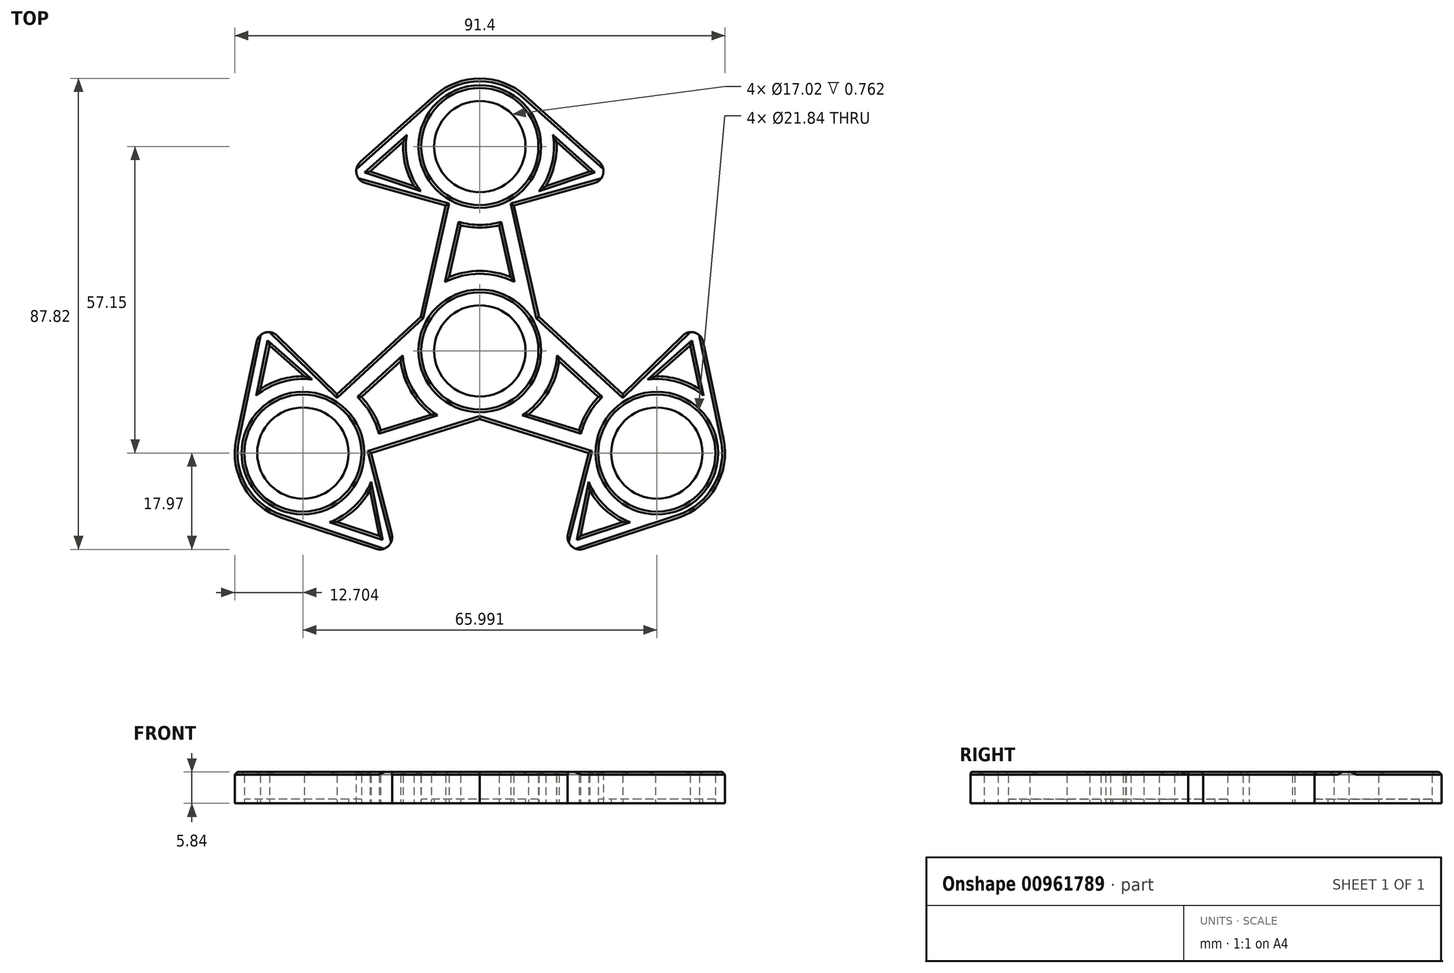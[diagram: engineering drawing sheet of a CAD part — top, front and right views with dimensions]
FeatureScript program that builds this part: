
annotation { "Feature Type Name" : "Feature", "Feature Type Description" : "" }
export const myFeature = defineFeature(function(context is Context, id is Id, definition is map)
    precondition{}
    {
        {
            var Q0;
            Q0=qCreatedBy(makeId("Top.planeOp"),FACE);
            var sketch = newSketch(context, id + "F0", { "sketchPlane" : qUnion([Q0])});
            skCircle(sketch, "E0", {"center": v(0, 0) * mm, "radius": 10.92 * mm});
            skCircle(sketch, "E1", {"center": v(0, 38.1) * mm, "radius": 10.92 * mm});
            skArc(sketch, "E2", {"start": v(8.46, 47.57) * mm, "mid": v(0, 50.8) * mm, "end": v(-8.46, 47.57) * mm});
            skCircle(sketch, "E3.1.1", {"center": v(-33, -19.05) * mm, "radius": 10.92 * mm});
            skArc(sketch, "E3.1.3", {"start": v(-45.43, -16.45) * mm, "mid": v(-44, -25.4) * mm, "end": v(-36.96, -31.11) * mm});
            skCircle(sketch, "E3.2.1", {"center": v(33, -19.05) * mm, "radius": 10.92 * mm});
            skArc(sketch, "E3.2.3", {"start": v(36.96, -31.11) * mm, "mid": v(44, -25.4) * mm, "end": v(45.43, -16.45) * mm});
            skLineSegment(sketch, "E4", {"start": v(0, 0) * mm, "end": v(0, 38.1) * mm});
            skLineSegment(sketch, "E5", {"start": v(-25.4, 32.43) * mm, "end": v(-8.46, 47.57) * mm});
            skLineSegment(sketch, "E6", {"start": v(8.46, 47.57) * mm, "end": v(25.4, 32.43) * mm});
            skLineSegment(sketch, "E7", {"start": v(25.4, 32.43) * mm, "end": v(6.35, 27.1) * mm});
            skLineSegment(sketch, "E8", {"start": v(-6.35, 27.1) * mm, "end": v(-25.4, 32.43) * mm});
            skLineSegment(sketch, "E9.1.0", {"start": v(-15.39, -38.21) * mm, "end": v(-36.96, -31.11) * mm});
            skLineSegment(sketch, "E9.2.0", {"start": v(40.79, 5.78) * mm, "end": v(45.43, -16.45) * mm});
            skLineSegment(sketch, "E10.1.0", {"start": v(-45.43, -16.45) * mm, "end": v(-40.79, 5.78) * mm});
            skLineSegment(sketch, "E10.2.0", {"start": v(36.96, -31.11) * mm, "end": v(15.39, -38.21) * mm});
            skLineSegment(sketch, "E11.1.0", {"start": v(-40.79, 5.78) * mm, "end": v(-26.65, -8.05) * mm});
            skLineSegment(sketch, "E11.2.0", {"start": v(15.39, -38.21) * mm, "end": v(20.3, -19.05) * mm});
            skLineSegment(sketch, "E12.1.0", {"start": v(-20.3, -19.05) * mm, "end": v(-15.39, -38.21) * mm});
            skLineSegment(sketch, "E12.2.0", {"start": v(26.65, -8.05) * mm, "end": v(40.79, 5.78) * mm});
            skLineSegment(sketch, "E13", {"start": v(-6.35, 27.1) * mm, "end": v(-11, 6.35) * mm});
            skLineSegment(sketch, "E14", {"start": v(-11, 6.35) * mm, "end": v(-26.65, -8.05) * mm});
            skLineSegment(sketch, "E15", {"start": v(-20.3, -19.05) * mm, "end": v(0, -12.7) * mm});
            skLineSegment(sketch, "E16", {"start": v(0, -12.7) * mm, "end": v(20.3, -19.05) * mm});
            skLineSegment(sketch, "E17", {"start": v(26.65, -8.05) * mm, "end": v(11, 6.35) * mm});
            skLineSegment(sketch, "E18", {"start": v(11, 6.35) * mm, "end": v(6.35, 27.1) * mm});
            skLineSegment(sketch, "E19", {"start": v(-14.29, 39.01) * mm, "end": v(-20.47, 33.49) * mm});
            skLineSegment(sketch, "E20", {"start": v(-20.47, 33.49) * mm, "end": v(-12.27, 30.72) * mm});
            skLineSegment(sketch, "E21", {"start": v(12.27, 30.72) * mm, "end": v(20.47, 33.49) * mm});
            skLineSegment(sketch, "E22", {"start": v(20.47, 33.49) * mm, "end": v(14.29, 39.01) * mm});
            skLineSegment(sketch, "E23.1.0", {"start": v(-26.64, -31.88) * mm, "end": v(-18.76, -34.47) * mm});
            skLineSegment(sketch, "E23.2.0", {"start": v(40.93, -7.13) * mm, "end": v(39.24, 0.98) * mm});
            skLineSegment(sketch, "E24.1.0", {"start": v(-18.76, -34.47) * mm, "end": v(-20.47, -25.98) * mm});
            skLineSegment(sketch, "E24.2.0", {"start": v(39.24, 0.98) * mm, "end": v(32.73, -4.73) * mm});
            skLineSegment(sketch, "E25.1.0", {"start": v(-39.24, 0.99) * mm, "end": v(-40.93, -7.13) * mm});
            skLineSegment(sketch, "E25.2.0", {"start": v(18.76, -34.47) * mm, "end": v(26.64, -31.88) * mm});
            skLineSegment(sketch, "E26.1.0", {"start": v(-32.73, -4.73) * mm, "end": v(-39.24, 0.99) * mm});
            skLineSegment(sketch, "E26.2.0", {"start": v(20.47, -25.98) * mm, "end": v(18.76, -34.47) * mm});
            skLineSegment(sketch, "E27", {"start": v(-6.97, 24.32) * mm, "end": v(-7.06, 24.34) * mm});
            skLineSegment(sketch, "E28", {"start": v(6.97, 24.32) * mm, "end": v(7.06, 24.34) * mm});
            skArc(sketch, "E29", {"start": v(5.76, 13.75) * mm, "mid": v(0, 14.9) * mm, "end": v(-5.76, 13.75) * mm});
            skArc(sketch, "E30", {"start": v(-14.29, 39.01) * mm, "mid": v(-13.91, 34.7) * mm, "end": v(-12.27, 30.72) * mm});
            skArc(sketch, "E31.trimOffspring", {"start": v(12.27, 30.72) * mm, "mid": v(13.91, 34.71) * mm, "end": v(14.29, 39.01) * mm});
            skPoint(sketch, "E32.end.orphan", {"position": v(7.06, 23.94) * mm});
            skArc(sketch, "E33.trimOffspring", {"start": v(-3.59, 23.42) * mm, "mid": v(0, 23) * mm, "end": v(3.59, 23.42) * mm});
            skPoint(sketch, "E34.end.orphan", {"position": v(-7.06, 23.94) * mm});
            skPoint(sketch, "E35.orphan", {"position": v(13.84, 39.41) * mm});
            skPoint(sketch, "E36.orphan", {"position": v(-13.85, 39.4) * mm});
            skPoint(sketch, "E37.orphan", {"position": v(0, 30.72) * mm});
            skArc(sketch, "E38.trimOffspring", {"start": v(-14.78, -1.89) * mm, "mid": v(-12.9, -7.45) * mm, "end": v(-9.03, -11.86) * mm});
            skPoint(sketch, "E39.orphan", {"position": v(14.9, 0.4) * mm});
            skPoint(sketch, "E40.orphan", {"position": v(60.72, 26.83) * mm});
            skPoint(sketch, "E41.orphan", {"position": v(13.64, -1.78) * mm});
            skPoint(sketch, "E42.orphan", {"position": v(8.36, -10.92) * mm});
            skArc(sketch, "E43.trimOffspring", {"start": v(9.03, -11.86) * mm, "mid": v(12.9, -7.45) * mm, "end": v(14.78, -1.89) * mm});
            skPoint(sketch, "E44.orphan", {"position": v(-15.79, 1.94) * mm});
            skPoint(sketch, "E45.orphan", {"position": v(-8.36, -10.92) * mm});
            skPoint(sketch, "E46.orphan", {"position": v(-23.38, -7.4) * mm});
            skArc(sketch, "E47.1.0", {"start": v(-26.64, -31.88) * mm, "mid": v(-23.1, -29.4) * mm, "end": v(-20.47, -25.98) * mm});
            skArc(sketch, "E47.2.0", {"start": v(40.93, -7.13) * mm, "mid": v(37.01, -5.3) * mm, "end": v(32.73, -4.73) * mm});
            skArc(sketch, "E48.1.0", {"start": v(-32.73, -4.73) * mm, "mid": v(-37.02, -5.3) * mm, "end": v(-40.93, -7.13) * mm});
            skArc(sketch, "E48.2.0", {"start": v(20.47, -25.98) * mm, "mid": v(23.1, -29.4) * mm, "end": v(26.64, -31.88) * mm});
            skArc(sketch, "E49.1.0", {"start": v(-18.5, -14.82) * mm, "mid": v(-19.91, -11.5) * mm, "end": v(-22.08, -8.6) * mm});
            skArc(sketch, "E49.2.0", {"start": v(22.08, -8.6) * mm, "mid": v(19.91, -11.5) * mm, "end": v(18.5, -14.82) * mm});
            skPoint(sketch, "E50.orphan", {"position": v(-41.05, -7.72) * mm});
            skPoint(sketch, "E51.orphan", {"position": v(-27.2, -31.7) * mm});
            skPoint(sketch, "E52.orphan", {"position": v(27.2, -31.7) * mm});
            skPoint(sketch, "E53.orphan", {"position": v(41.05, -7.71) * mm});
            skLineSegment(sketch, "E54", {"start": v(-3.59, 23.42) * mm, "end": v(-5.76, 13.75) * mm});
            skLineSegment(sketch, "E55", {"start": v(3.59, 23.42) * mm, "end": v(5.76, 13.75) * mm});
            skPoint(sketch, "E56.orphan", {"position": v(-5.28, 23.94) * mm});
            skPoint(sketch, "E57.orphan", {"position": v(5.28, 23.94) * mm});
            skLineSegment(sketch, "E58.1.0", {"start": v(-18.5, -14.82) * mm, "end": v(-9.03, -11.86) * mm});
            skLineSegment(sketch, "E58.2.0", {"start": v(22.08, -8.6) * mm, "end": v(14.78, -1.89) * mm});
            skLineSegment(sketch, "E59.1.0", {"start": v(-22.08, -8.6) * mm, "end": v(-14.78, -1.89) * mm});
            skLineSegment(sketch, "E59.2.0", {"start": v(18.5, -14.82) * mm, "end": v(9.03, -11.86) * mm});
            skPoint(sketch, "E60.orphan", {"position": v(-18.1, -16.54) * mm});
            skPoint(sketch, "E61.orphan", {"position": v(23.38, -7.4) * mm});
            skPoint(sketch, "E62.orphan", {"position": v(18.1, -16.54) * mm});
            skCircle(sketch, "E63", {"center": v(0, 0) * mm, "radius": 8.5 * mm});
            skCircle(sketch, "E64", {"center": v(33, -19.05) * mm, "radius": 8.5 * mm});
            skCircle(sketch, "E65", {"center": v(-33, -19.05) * mm, "radius": 8.5 * mm});
            skCircle(sketch, "E66", {"center": v(0, 38.1) * mm, "radius": 8.5 * mm});
            skSolve(sketch);
        }
        {
            var Q0;
            Q0=makeQuery(id+"F0.imprint","IMPRINT",FACE,{"disambiguationData":[TD([[makeQuery(id+"F0.imprint","IMPRINT",EDGE,{"derivedFrom":sQuery(id+"F0.wireOp",EDGE,"E0")}),1.0]])]});
            var Q1;
            Q1=makeQuery(id+"F0.imprint","IMPRINT",FACE,{"disambiguationData":[TD([[makeQuery(id+"F0.imprint","IMPRINT",EDGE,{"derivedFrom":sQuery(id+"F0.wireOp",EDGE,"E3.2.1")}),1.0]])]});
            var Q2;
            Q2=makeQuery(id+"F0.imprint","IMPRINT",FACE,{"disambiguationData":[TD([[makeQuery(id+"F0.imprint","IMPRINT",EDGE,{"derivedFrom":sQuery(id+"F0.wireOp",EDGE,"E1")}),1.0]])]});
            var Q3;
            Q3=makeQuery(id+"F0.imprint","IMPRINT",FACE,{"disambiguationData":[TD([[makeQuery(id+"F0.imprint","IMPRINT",EDGE,{"derivedFrom":sQuery(id+"F0.wireOp",EDGE,"E3.1.1")}),1.0]])]});
            extrude(context, id + "F1", {"entities" : qUnion([Q0, Q1, Q2, Q3]), "depth" : 0.76 * mm, "offsetDistance" : 25.4 * mm});
        }
        {
            var Q0;
            Q0=makeQuery(id+"F0.imprint","IMPRINT",FACE,{"disambiguationData":[TD([[makeQuery(id+"F0.imprint","IMPRINT",EDGE,{"derivedFrom":sQuery(id+"F0.wireOp",EDGE,"E0")}),-1.0]])]});
            var Q1;
            {var subQ0=sQuery(id+"F0.wireOp",EDGE,"E3.2.2");Q1=makeQuery(id+"F0.imprint","IMPRINT",FACE,{"disambiguationData":[TD([[makeQuery(id+"F0.imprint","IMPRINT",EDGE,{"derivedFrom":subQ0}),1.0]])]});}
            var Q2;
            {var subQ0=sQuery(id+"F0.wireOp",EDGE,"qAN6bfDQ-EvD6-PB0c-LLV5-TB6usP3qM8oL");Q2=makeQuery(id+"F0.imprint","IMPRINT",FACE,{"disambiguationData":[TD([[makeQuery(id+"F0.imprint","IMPRINT",EDGE,{"derivedFrom":subQ0}),1.0]])]});}
            var Q3;
            {var subQ0=sQuery(id+"F0.wireOp",EDGE,"E3.1.2");Q3=makeQuery(id+"F0.imprint","IMPRINT",FACE,{"disambiguationData":[TD([[makeQuery(id+"F0.imprint","IMPRINT",EDGE,{"derivedFrom":subQ0}),1.0]])]});}
            var Q4;
            {var subQ0=sQuery(id+"F0.wireOp",EDGE,"9fF8XZbd-x6Pi-r7dD-wS89-5iYDqfJ158Ww");Q4=makeQuery(id+"F0.imprint","IMPRINT",FACE,{"disambiguationData":[TD([[makeQuery(id+"F0.imprint","IMPRINT",EDGE,{"derivedFrom":subQ0}),-1.0]])]});}
            var Q5;
            {var subQ0=sQuery(id+"F0.wireOp",EDGE,"6K4n1ReX-d9US-5ZDi-A2DK-j992RhachGyF");Q5=makeQuery(id+"F0.imprint","IMPRINT",FACE,{"disambiguationData":[TD([[makeQuery(id+"F0.imprint","IMPRINT",EDGE,{"derivedFrom":subQ0}),1.0]])]});}
            var Q6;
            Q6=makeQuery(id+"F0.imprint","IMPRINT",FACE,{"disambiguationData":[TD([[makeQuery(id+"F0.imprint","IMPRINT",EDGE,{"derivedFrom":sQuery(id+"F0.wireOp",EDGE,"E2")}),1.0]])]});
            var Q7;
            {var subQ0=sQuery(id+"F0.wireOp",EDGE,"9fF8XZbd-x6Pi-r7dD-wS89-5iYDqfJ158Ww");Q7=makeQuery(id+"F0.imprint","IMPRINT",FACE,{"disambiguationData":[TD([[makeQuery(id+"F0.imprint","IMPRINT",EDGE,{"derivedFrom":subQ0}),1.0]])]});}
            var Q8;
            {var subQ0=sQuery(id+"F0.wireOp",EDGE,"qAN6bfDQ-EvD6-PB0c-LLV5-TB6usP3qM8oL");Q8=makeQuery(id+"F0.imprint","IMPRINT",FACE,{"disambiguationData":[TD([[makeQuery(id+"F0.imprint","IMPRINT",EDGE,{"derivedFrom":subQ0}),-1.0]])]});}
            var Q9;
            {var subQ0=sQuery(id+"F0.wireOp",EDGE,"Vkq1GlN2-p2l9-0JIi-93ZN-x3V1hNP8lanI");var subQ1=sQuery(id+"F0.wireOp",EDGE,"OuJw4BYg-WvBj-6tcM-ZUpN-g2h8ElnBMkLZ");var subQ2=makeQuery(id+"F0.imprint","INTERSECT",VERTEX,{"derivedFrom":[subQ1,subQ0]});Q9=makeQuery(id+"F0.imprint","IMPRINT",FACE,{"disambiguationData":[TD([[makeQuery(id+"F0.imprint","IMPRINT",EDGE,{"disambiguationData":[TD([[subQ2,-1.0]])],"derivedFrom":subQ0}),1.0]])]});}
            var Q10;
            {var subQ1=sQuery(id+"F0.wireOp",EDGE,"45f8ba8a-7cd9-4461-8c1c-9691e63ae262.trimOffspring");var subQ5=sQuery(id+"F0.wireOp",EDGE,"TcN3lwoU-SvPN-Eq9K-OPf6-Ab366GjWDurW");var subQ8=makeQuery(id+"F0.imprint","INTERSECT",VERTEX,{"derivedFrom":[subQ5,subQ1]});Q10=makeQuery(id+"F0.imprint","IMPRINT",FACE,{"disambiguationData":[TD([[makeQuery(id+"F0.imprint","IMPRINT",EDGE,{"disambiguationData":[TD([[subQ8,-1.0]])],"derivedFrom":subQ5}),-1.0]])]});}
            var Q11;
            Q11=makeQuery(id+"F0.imprint","IMPRINT",FACE,{"disambiguationData":[TD([[makeQuery(id+"F0.imprint","IMPRINT",EDGE,{"derivedFrom":sQuery(id+"F0.wireOp",EDGE,"E5")}),-1.0]])]});
            var Q12;
            Q12=makeQuery(id+"F0.imprint","IMPRINT",FACE,{"disambiguationData":[TD([[makeQuery(id+"F0.imprint","IMPRINT",EDGE,{"derivedFrom":sQuery(id+"F0.wireOp",EDGE,"E6")}),-1.0]])]});
            var Q13;
            {var subQ0=sQuery(id+"F0.wireOp",EDGE,"PzGggORM-jraf-rS0D-nCfz-ZiBeTToQzrcL");Q13=makeQuery(id+"F0.imprint","IMPRINT",FACE,{"disambiguationData":[TD([[makeQuery(id+"F0.imprint","IMPRINT",EDGE,{"derivedFrom":subQ0}),1.0]])]});}
            var Q14;
            Q14=makeQuery(id+"F0.imprint","IMPRINT",FACE,{"disambiguationData":[TD([[makeQuery(id+"F0.imprint","IMPRINT",EDGE,{"derivedFrom":sQuery(id+"F0.wireOp",EDGE,"E3.2.1")}),-1.0]])]});
            var Q15;
            {var subQ3=sQuery(id+"F0.wireOp",EDGE,"9a17e62f-96f6-4f13-b012-882fd0498e39.2.0");var subQ5=sQuery(id+"F0.wireOp",EDGE,"06a4b1de-04c7-4eba-a49c-bad1cd3fa0e8.2.0");var subQ7=makeQuery(id+"F0.imprint","INTERSECT",VERTEX,{"derivedFrom":[subQ3,subQ5]});Q15=makeQuery(id+"F0.imprint","IMPRINT",FACE,{"disambiguationData":[TD([[makeQuery(id+"F0.imprint","IMPRINT",EDGE,{"disambiguationData":[TD([[subQ7,1.0]])],"derivedFrom":subQ3}),1.0]])]});}
            var Q16;
            Q16=makeQuery(id+"F0.imprint","IMPRINT",FACE,{"disambiguationData":[TD([[makeQuery(id+"F0.imprint","IMPRINT",EDGE,{"derivedFrom":sQuery(id+"F0.wireOp",EDGE,"E3.1.1")}),-1.0]])]});
            var Q17;
            {var subQ3=sQuery(id+"F0.wireOp",EDGE,"9a17e62f-96f6-4f13-b012-882fd0498e39.1.0");var subQ5=sQuery(id+"F0.wireOp",EDGE,"06a4b1de-04c7-4eba-a49c-bad1cd3fa0e8.1.0");var subQ7=makeQuery(id+"F0.imprint","INTERSECT",VERTEX,{"derivedFrom":[subQ3,subQ5]});Q17=makeQuery(id+"F0.imprint","IMPRINT",FACE,{"disambiguationData":[TD([[makeQuery(id+"F0.imprint","IMPRINT",EDGE,{"disambiguationData":[TD([[subQ7,1.0]])],"derivedFrom":subQ3}),1.0]])]});}
            var Q18;
            {var subQ2=sQuery(id+"F0.wireOp",EDGE,"E3.1.0");var subQ5=sQuery(id+"F0.wireOp",EDGE,"OuJw4BYg-WvBj-6tcM-ZUpN-g2h8ElnBMkLZ");var subQ8=makeQuery(id+"F0.imprint","INTERSECT",VERTEX,{"derivedFrom":[subQ5,subQ2]});Q18=makeQuery(id+"F0.imprint","IMPRINT",FACE,{"disambiguationData":[TD([[makeQuery(id+"F0.imprint","IMPRINT",EDGE,{"disambiguationData":[TD([[subQ8,-1.0]])],"derivedFrom":subQ2}),-1.0]])]});}
            var Q19;
            {var subQ3=sQuery(id+"F0.wireOp",EDGE,"Yt0YYVHN-KNV7-8yMq-8hyP-T0BDWzkc9sLh");Q19=makeQuery(id+"F0.imprint","IMPRINT",FACE,{"disambiguationData":[TD([[makeQuery(id+"F0.imprint","IMPRINT",EDGE,{"derivedFrom":subQ3}),-1.0]])]});}
            var Q20;
            {var subQ2=sQuery(id+"F0.wireOp",EDGE,"E3.2.0");var subQ5=sQuery(id+"F0.wireOp",EDGE,"e03ed8af-40f6-4605-b513-6e7bd98e8c99.trimOffspring");var subQ8=makeQuery(id+"F0.imprint","INTERSECT",VERTEX,{"derivedFrom":[subQ2,subQ5]});Q20=makeQuery(id+"F0.imprint","IMPRINT",FACE,{"disambiguationData":[TD([[makeQuery(id+"F0.imprint","IMPRINT",EDGE,{"disambiguationData":[TD([[subQ8,-1.0]])],"derivedFrom":subQ2}),-1.0]])]});}
            var Q21;
            {var subQ1=sQuery(id+"F0.wireOp",EDGE,"E13");var subQ3=sQuery(id+"F0.wireOp",EDGE,"E27");var subQ4=makeQuery(id+"F0.imprint","INTERSECT",VERTEX,{"derivedFrom":[subQ1,subQ3]});Q21=makeQuery(id+"F0.imprint","IMPRINT",FACE,{"disambiguationData":[TD([[makeQuery(id+"F0.imprint","IMPRINT",EDGE,{"disambiguationData":[TD([[subQ4,1.0]])],"derivedFrom":subQ3}),-1.0]])]});}
            var Q22;
            {var subQ0=sQuery(id+"F0.wireOp",EDGE,"E34");var subQ1=sQuery(id+"F0.wireOp",EDGE,"E13");var subQ2=makeQuery(id+"F0.imprint","INTERSECT",VERTEX,{"derivedFrom":[subQ1,subQ0]});Q22=makeQuery(id+"F0.imprint","IMPRINT",FACE,{"disambiguationData":[TD([[makeQuery(id+"F0.imprint","IMPRINT",EDGE,{"disambiguationData":[TD([[subQ2,1.0]])],"derivedFrom":subQ1}),1.0]])]});}
            var Q23;
            {var subQ0=sQuery(id+"F0.wireOp",EDGE,"E34");var subQ1=sQuery(id+"F0.wireOp",EDGE,"E13");var subQ2=makeQuery(id+"F0.imprint","INTERSECT",VERTEX,{"derivedFrom":[subQ1,subQ0]});Q23=makeQuery(id+"F0.imprint","IMPRINT",FACE,{"disambiguationData":[TD([[makeQuery(id+"F0.imprint","IMPRINT",EDGE,{"disambiguationData":[TD([[subQ2,-1.0]])],"derivedFrom":subQ1}),1.0]])]});}
            var Q24;
            {var subQ1=sQuery(id+"F0.wireOp",EDGE,"E34");var subQ3=sQuery(id+"F0.wireOp",EDGE,"b4e95768-ea4a-4253-9161-41f6c7fc2a35.trimOffspring");var subQ4=makeQuery(id+"F0.imprint","INTERSECT",VERTEX,{"derivedFrom":[subQ1,subQ3]});Q24=makeQuery(id+"F0.imprint","IMPRINT",FACE,{"disambiguationData":[TD([[makeQuery(id+"F0.imprint","IMPRINT",EDGE,{"disambiguationData":[TD([[subQ4,-1.0]])],"derivedFrom":subQ3}),-1.0]])]});}
            var Q25;
            {var subQ0=sQuery(id+"F0.wireOp",EDGE,"E32");var subQ1=sQuery(id+"F0.wireOp",EDGE,"E18");var subQ2=makeQuery(id+"F0.imprint","INTERSECT",VERTEX,{"derivedFrom":[subQ1,subQ0]});Q25=makeQuery(id+"F0.imprint","IMPRINT",FACE,{"disambiguationData":[TD([[makeQuery(id+"F0.imprint","IMPRINT",EDGE,{"disambiguationData":[TD([[subQ2,-1.0]])],"derivedFrom":subQ1}),1.0]])]});}
            var Q26;
            {var subQ1=sQuery(id+"F0.wireOp",EDGE,"E32");var subQ3=sQuery(id+"F0.wireOp",EDGE,"2032d7e4-90d3-44b6-8336-25ac22edd1a0.trimOffspring");var subQ4=makeQuery(id+"F0.imprint","INTERSECT",VERTEX,{"derivedFrom":[subQ1,subQ3]});Q26=makeQuery(id+"F0.imprint","IMPRINT",FACE,{"disambiguationData":[TD([[makeQuery(id+"F0.imprint","IMPRINT",EDGE,{"disambiguationData":[TD([[subQ4,-1.0]])],"derivedFrom":subQ3}),1.0]])]});}
            var Q27;
            {var subQ1=sQuery(id+"F0.wireOp",EDGE,"E18");var subQ3=sQuery(id+"F0.wireOp",EDGE,"E28");var subQ4=makeQuery(id+"F0.imprint","INTERSECT",VERTEX,{"derivedFrom":[subQ1,subQ3]});Q27=makeQuery(id+"F0.imprint","IMPRINT",FACE,{"disambiguationData":[TD([[makeQuery(id+"F0.imprint","IMPRINT",EDGE,{"disambiguationData":[TD([[subQ4,1.0]])],"derivedFrom":subQ3}),1.0]])]});}
            extrude(context, id + "F2", {"entities" : qUnion([Q0, Q1, Q2, Q3, Q4, Q5, Q6, Q7, Q8, Q9, Q10, Q11, Q12, Q13, Q14, Q15, Q16, Q17, Q18, Q19, Q20, Q21, Q22, Q23, Q24, Q25, Q26, Q27]), "depth" : 5.84 * mm, "offsetDistance" : 25.4 * mm});
        }
        {
            var Q0;
            Q0=makeQuery(id+"F2.opExtrude","CAP_FACE",FACE,{"disambiguationData":[OSD([sQuery(id+"F0.wireOp",EDGE,"E0"),sQuery(id+"F0.wireOp",EDGE,"E1"),sQuery(id+"F0.wireOp",EDGE,"E2"),sQuery(id+"F0.wireOp",EDGE,"E3.1.1"),sQuery(id+"F0.wireOp",EDGE,"E3.1.3"),sQuery(id+"F0.wireOp",EDGE,"E3.2.1"),sQuery(id+"F0.wireOp",EDGE,"E3.2.3"),sQuery(id+"F0.wireOp",EDGE,"E5"),sQuery(id+"F0.wireOp",EDGE,"E6"),sQuery(id+"F0.wireOp",EDGE,"E7"),sQuery(id+"F0.wireOp",EDGE,"E8"),sQuery(id+"F0.wireOp",EDGE,"E9.1.0"),sQuery(id+"F0.wireOp",EDGE,"E9.2.0"),sQuery(id+"F0.wireOp",EDGE,"E10.1.0"),sQuery(id+"F0.wireOp",EDGE,"E10.2.0"),sQuery(id+"F0.wireOp",EDGE,"E11.1.0"),sQuery(id+"F0.wireOp",EDGE,"E11.2.0"),sQuery(id+"F0.wireOp",EDGE,"E12.1.0"),sQuery(id+"F0.wireOp",EDGE,"E12.2.0"),sQuery(id+"F0.wireOp",EDGE,"E13"),sQuery(id+"F0.wireOp",EDGE,"E14"),sQuery(id+"F0.wireOp",EDGE,"E15"),sQuery(id+"F0.wireOp",EDGE,"E16"),sQuery(id+"F0.wireOp",EDGE,"E17"),sQuery(id+"F0.wireOp",EDGE,"E18"),sQuery(id+"F0.wireOp",EDGE,"E19"),sQuery(id+"F0.wireOp",EDGE,"E20"),sQuery(id+"F0.wireOp",EDGE,"E21"),sQuery(id+"F0.wireOp",EDGE,"E22"),sQuery(id+"F0.wireOp",EDGE,"E23.1.0"),sQuery(id+"F0.wireOp",EDGE,"E23.2.0"),sQuery(id+"F0.wireOp",EDGE,"E24.1.0"),sQuery(id+"F0.wireOp",EDGE,"E24.2.0"),sQuery(id+"F0.wireOp",EDGE,"E25.1.0"),sQuery(id+"F0.wireOp",EDGE,"E25.2.0"),sQuery(id+"F0.wireOp",EDGE,"E26.1.0"),sQuery(id+"F0.wireOp",EDGE,"E26.2.0"),sQuery(id+"F0.wireOp",EDGE,"E29"),sQuery(id+"F0.wireOp",EDGE,"E30"),sQuery(id+"F0.wireOp",EDGE,"E31.trimOffspring"),sQuery(id+"F0.wireOp",EDGE,"E33.trimOffspring"),sQuery(id+"F0.wireOp",EDGE,"E47.1.0"),sQuery(id+"F0.wireOp",EDGE,"E47.2.0"),sQuery(id+"F0.wireOp",EDGE,"E48.1.0"),sQuery(id+"F0.wireOp",EDGE,"E48.2.0"),sQuery(id+"F0.wireOp",EDGE,"E54"),sQuery(id+"F0.wireOp",EDGE,"E55"),sQuery(id+"F0.wireOp",EDGE,"E49.1.0"),sQuery(id+"F0.wireOp",EDGE,"E49.2.0"),sQuery(id+"F0.wireOp",EDGE,"E38.trimOffspring"),sQuery(id+"F0.wireOp",EDGE,"E43.trimOffspring"),sQuery(id+"F0.wireOp",EDGE,"E58.1.0"),sQuery(id+"F0.wireOp",EDGE,"E58.2.0"),sQuery(id+"F0.wireOp",EDGE,"E59.1.0"),sQuery(id+"F0.wireOp",EDGE,"E59.2.0")])],"isStart":false});
            chamfer(context, id + "F3", {"entities" : qUnion([Q0]), "width" : 0.5 * mm, "tangentPropagation" : true});
        }
        {
            var Q0;
            Q0=makeQuery(id+"F2.opExtrude","SWEPT_EDGE",EDGE,{"disambiguationData":[OSD([sQuery(id+"F0.wireOp",EDGE,"E10.1.0"),sQuery(id+"F0.wireOp",EDGE,"E11.1.0")])]});
            var Q1;
            Q1=makeQuery(id+"F2.opExtrude","SWEPT_EDGE",EDGE,{"disambiguationData":[OSD([sQuery(id+"F0.wireOp",EDGE,"E5"),sQuery(id+"F0.wireOp",EDGE,"E8")])]});
            var Q2;
            Q2=makeQuery(id+"F2.opExtrude","SWEPT_EDGE",EDGE,{"disambiguationData":[OSD([sQuery(id+"F0.wireOp",EDGE,"E6"),sQuery(id+"F0.wireOp",EDGE,"E7")])]});
            var Q3;
            Q3=makeQuery(id+"F2.opExtrude","SWEPT_EDGE",EDGE,{"disambiguationData":[OSD([sQuery(id+"F0.wireOp",EDGE,"E9.2.0"),sQuery(id+"F0.wireOp",EDGE,"E12.2.0")])]});
            var Q4;
            Q4=makeQuery(id+"F2.opExtrude","SWEPT_EDGE",EDGE,{"disambiguationData":[OSD([sQuery(id+"F0.wireOp",EDGE,"E10.2.0"),sQuery(id+"F0.wireOp",EDGE,"E11.2.0")])]});
            var Q5;
            Q5=makeQuery(id+"F2.opExtrude","SWEPT_EDGE",EDGE,{"disambiguationData":[OSD([sQuery(id+"F0.wireOp",EDGE,"E9.1.0"),sQuery(id+"F0.wireOp",EDGE,"E12.1.0")])]});
            fillet(context, id + "F4", {"entities" : qUnion([Q0, Q1, Q2, Q3, Q4, Q5]), "radius" : 2.3 * mm, "tangentPropagation" : true, "allowEdgeOverflow" : false});
        }
    });
